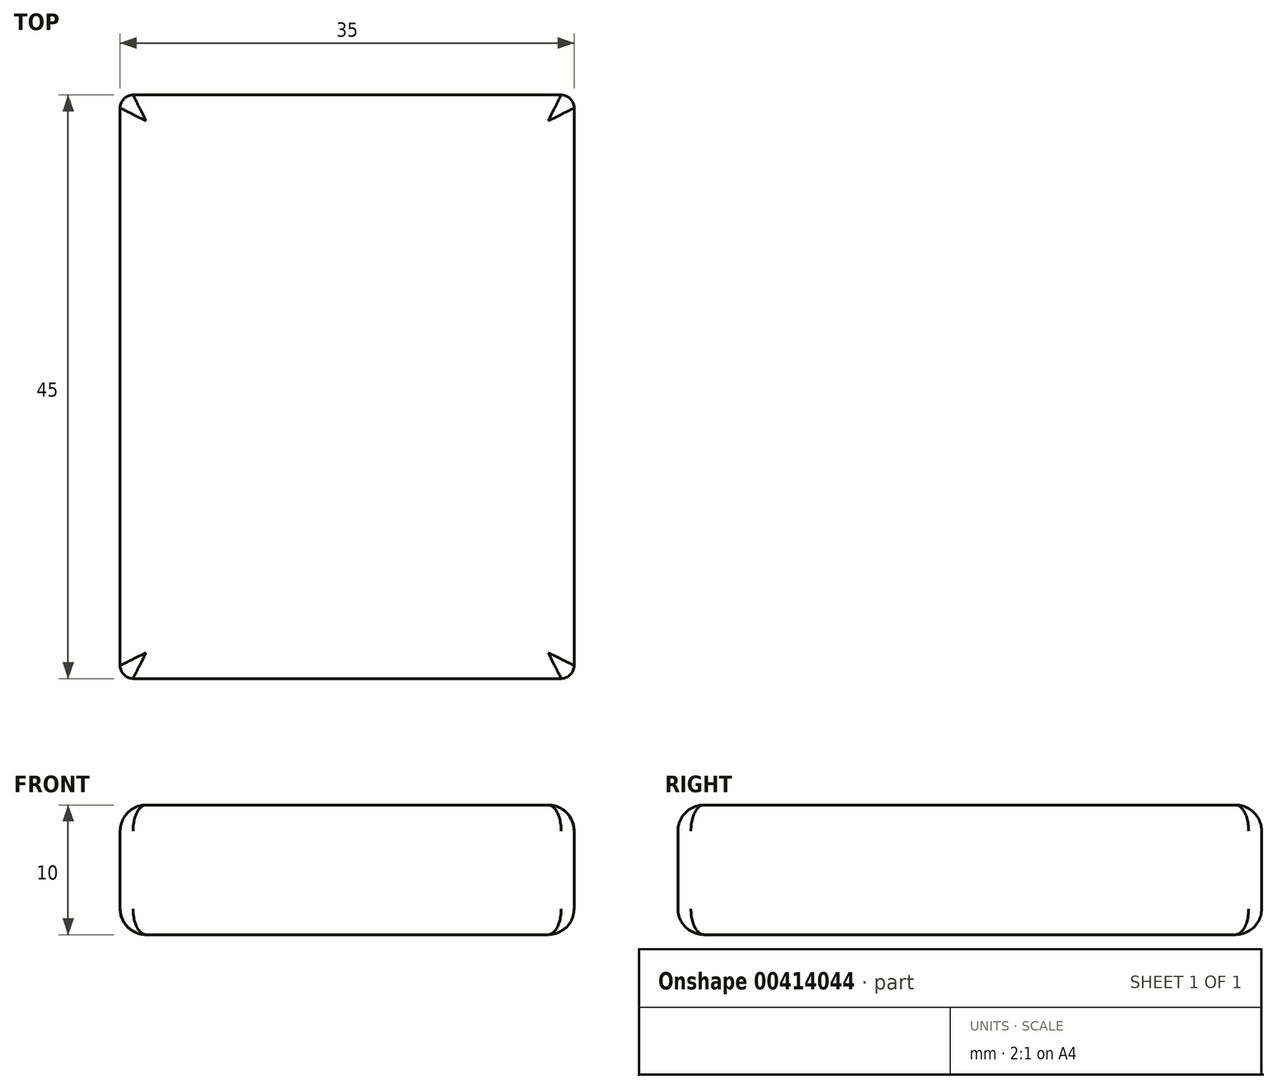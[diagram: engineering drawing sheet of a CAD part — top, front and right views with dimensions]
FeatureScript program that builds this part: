
annotation { "Feature Type Name" : "Feature", "Feature Type Description" : "" }
export const myFeature = defineFeature(function(context is Context, id is Id, definition is map)
    precondition{}
    {
        {
            var Q0;
            Q0=qCreatedBy(makeId("Top.planeOp"),FACE);
            var sketch = newSketch(context, id + "F0", { "sketchPlane" : qUnion([Q0])});
            skLineSegment(sketch, "E0.bottom", {"start": v(17.5, 22.5) * mm, "end": v(-17.5, 22.5) * mm});
            skLineSegment(sketch, "E0.top", {"start": v(17.5, -22.5) * mm, "end": v(-17.5, -22.5) * mm});
            skLineSegment(sketch, "E0.left", {"start": v(17.5, 22.5) * mm, "end": v(17.5, -22.5) * mm});
            skLineSegment(sketch, "E0.right", {"start": v(-17.5, 22.5) * mm, "end": v(-17.5, -22.5) * mm});
            skPoint(sketch, "E0.middle", {"position": v(0, 0) * mm});
            skSolve(sketch);
        }
        {
            var Q0;
            Q0 = qSketchRegion(id + "F0", true);
            extrude(context, id + "F1", {"entities" : qUnion([Q0]), "depth" : 10 * mm});
        }
        {
            var Q0;
            Q0=makeQuery(id+"F1.opExtrude","CAP_EDGE",EDGE,{"disambiguationData":[OSD([sQuery(id+"F0.wireOp",EDGE,"E0.left")])],"isStart":false});
            var Q1;
            Q1=makeQuery(id+"F1.opExtrude","CAP_EDGE",EDGE,{"disambiguationData":[OSD([sQuery(id+"F0.wireOp",EDGE,"E0.left")])],"isStart":true});
            var Q2;
            Q2=makeQuery(id+"F1.opExtrude","CAP_EDGE",EDGE,{"disambiguationData":[OSD([sQuery(id+"F0.wireOp",EDGE,"E0.right")])],"isStart":false});
            var Q3;
            Q3=makeQuery(id+"F1.opExtrude","CAP_EDGE",EDGE,{"disambiguationData":[OSD([sQuery(id+"F0.wireOp",EDGE,"E0.right")])],"isStart":true});
            var Q4;
            Q4=makeQuery(id+"F1.opExtrude","CAP_EDGE",EDGE,{"disambiguationData":[OSD([sQuery(id+"F0.wireOp",EDGE,"E0.top")])],"isStart":false});
            var Q5;
            Q5=makeQuery(id+"F1.opExtrude","CAP_EDGE",EDGE,{"disambiguationData":[OSD([sQuery(id+"F0.wireOp",EDGE,"E0.bottom")])],"isStart":false});
            var Q6;
            Q6=makeQuery(id+"F1.opExtrude","CAP_EDGE",EDGE,{"disambiguationData":[OSD([sQuery(id+"F0.wireOp",EDGE,"E0.top")])],"isStart":true});
            var Q7;
            Q7=makeQuery(id+"F1.opExtrude","CAP_EDGE",EDGE,{"disambiguationData":[OSD([sQuery(id+"F0.wireOp",EDGE,"E0.bottom")])],"isStart":true});
            fillet(context, id + "F2", {"entities" : qUnion([Q0, Q1, Q2, Q3, Q4, Q5, Q6, Q7]), "radius" : 2 * mm, "tangentPropagation" : true, "allowEdgeOverflow" : false});
        }
        {
            var Q0;
            Q0=makeQuery(id+"F1.opExtrude","SWEPT_EDGE",EDGE,{"disambiguationData":[OSD([sQuery(id+"F0.wireOp",EDGE,"E0.top"),sQuery(id+"F0.wireOp",EDGE,"E0.left")])]});
            var Q1;
            Q1=makeQuery(id+"F1.opExtrude","SWEPT_EDGE",EDGE,{"disambiguationData":[OSD([sQuery(id+"F0.wireOp",EDGE,"E0.top"),sQuery(id+"F0.wireOp",EDGE,"E0.right")])]});
            var Q2;
            Q2=makeQuery(id+"F1.opExtrude","SWEPT_EDGE",EDGE,{"disambiguationData":[OSD([sQuery(id+"F0.wireOp",EDGE,"E0.bottom"),sQuery(id+"F0.wireOp",EDGE,"E0.left")])]});
            var Q3;
            Q3=makeQuery(id+"F1.opExtrude","SWEPT_EDGE",EDGE,{"disambiguationData":[OSD([sQuery(id+"F0.wireOp",EDGE,"E0.bottom"),sQuery(id+"F0.wireOp",EDGE,"E0.right")])]});
            fillet(context, id + "F3", {"entities" : qUnion([Q0, Q1, Q2, Q3]), "radius" : 1 * mm, "tangentPropagation" : true, "allowEdgeOverflow" : false});
        }
    });
